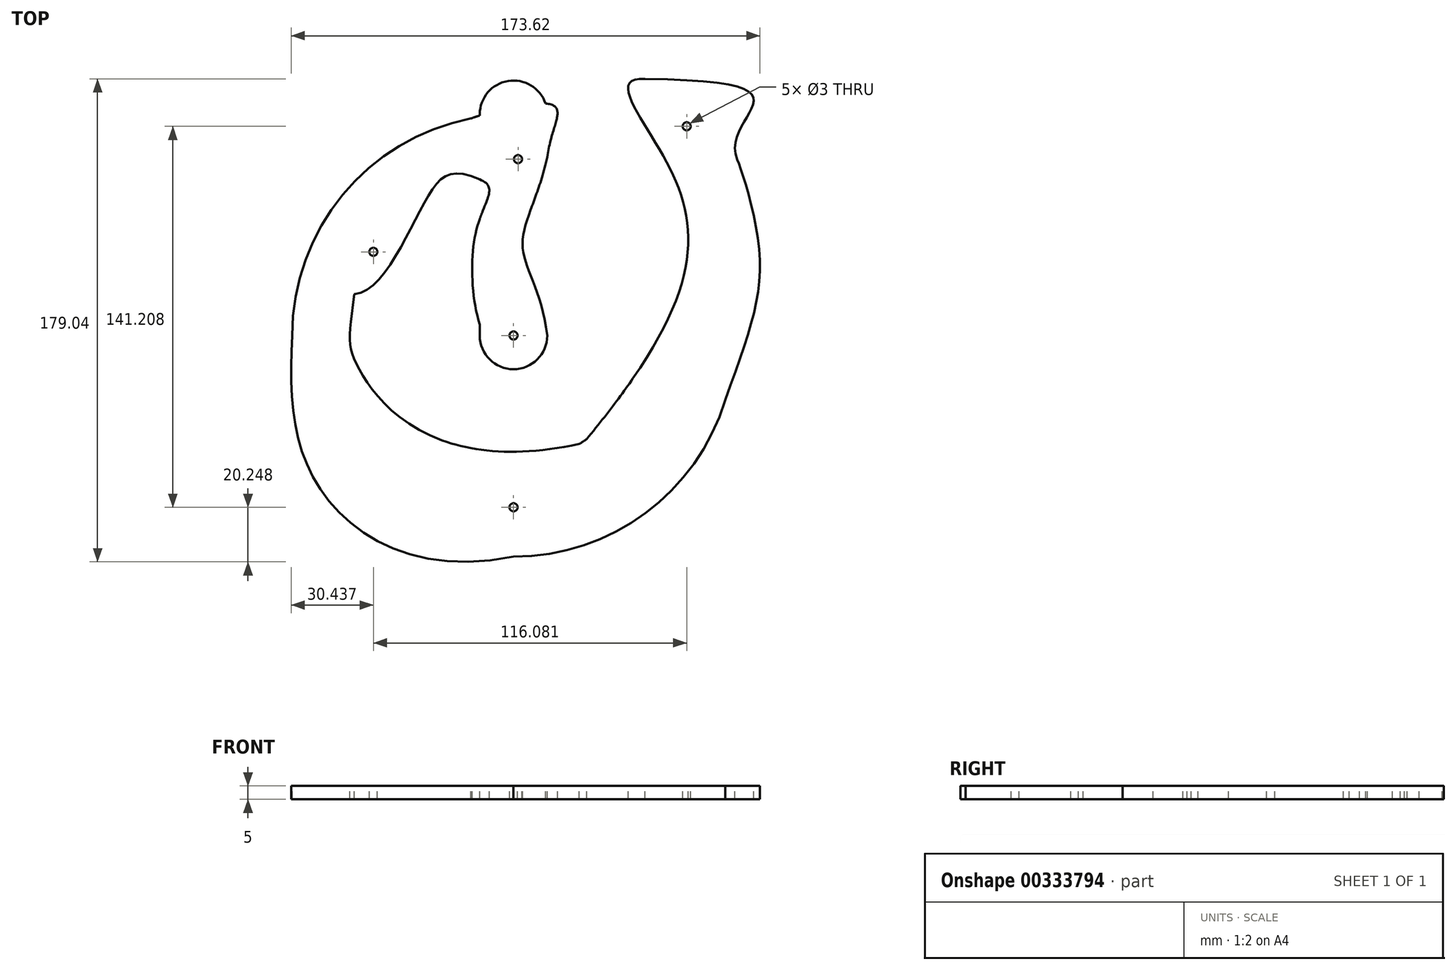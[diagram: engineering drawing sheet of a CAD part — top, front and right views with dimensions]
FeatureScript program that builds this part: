
annotation { "Feature Type Name" : "Feature", "Feature Type Description" : "" }
export const myFeature = defineFeature(function(context is Context, id is Id, definition is map)
    precondition{}
    {
        {
            var Q0;
            Q0=qCreatedBy(makeId("Top.planeOp"),FACE);
            var sketch = newSketch(context, id + "F0", { "sketchPlane" : qUnion([Q0])});
            skLineSegment(sketch, "E0.bottom", {"start": v(100, 100) * mm, "end": v(-100, 100) * mm});
            skLineSegment(sketch, "E0.top", {"start": v(100, -100) * mm, "end": v(-100, -100) * mm});
            skLineSegment(sketch, "E0.left", {"start": v(100, 100) * mm, "end": v(100, -100) * mm});
            skLineSegment(sketch, "E0.right", {"start": v(-100, 100) * mm, "end": v(-100, -100) * mm});
            skPoint(sketch, "E0.middle", {"position": v(0, 0) * mm});
            skSolve(sketch);
        }
        {
            var Q0;
            Q0=qSketchRegion(id+"F0",true);
            extrude(context, id + "F1", {"entities" : qUnion([Q0]), "depth" : 5 * mm});
        }
        {
            var Q0;
            Q0=makeQuery(id+"F1.opExtrude","CAP_FACE",FACE,{"disambiguationData":[OSD([sQuery(id+"F0.wireOp",EDGE,"E0.bottom"),sQuery(id+"F0.wireOp",EDGE,"E0.top"),sQuery(id+"F0.wireOp",EDGE,"E0.left"),sQuery(id+"F0.wireOp",EDGE,"E0.right")])],"isStart":false});
            var sketch = newSketch(context, id + "F2", { "sketchPlane" : qUnion([Q0])});
            skCircle(sketch, "E1", {"center": v(0, 0) * mm, "radius": 1.5 * mm});
            skCircle(sketch, "E2", {"center": v(0, -63.66) * mm, "radius": 1.5 * mm});
            skCircle(sketch, "E3", {"center": v(64.16, 77.55) * mm, "radius": 1.5 * mm});
            skCircle(sketch, "E4", {"center": v(-51.92, 31.01) * mm, "radius": 1.5 * mm});
            skCircle(sketch, "E5", {"center": v(1.67, 65.37) * mm, "radius": 1.5 * mm});
            skSolve(sketch);
        }
        {
            var Q0;
            Q0=qSketchRegion(id+"F2",true);
            extrude(context, id + "F3", {"entities" : qUnion([Q0]), "operationType" : NewBodyOperationType.REMOVE, "endBound" : BoundingType.THROUGH_ALL, "oppositeDirection" : true, "depth" : 25 * mm});
        }
        {
            var Q0;
            Q0=makeQuery(id+"F1.opExtrude","CAP_FACE",FACE,{"disambiguationData":[OSD([sQuery(id+"F0.wireOp",EDGE,"E0.bottom"),sQuery(id+"F0.wireOp",EDGE,"E0.top"),sQuery(id+"F0.wireOp",EDGE,"E0.left"),sQuery(id+"F0.wireOp",EDGE,"E0.right")])],"isStart":false});
            var sketch = newSketch(context, id + "F4", { "sketchPlane" : qUnion([Q0])});
            skCircle(sketch, "E6", {"center": v(0, 0) * mm, "radius": 82 * mm});
            skCircle(sketch, "E7", {"center": v(0, 0) * mm, "radius": 47 * mm});
            skLineSegment(sketch, "E8", {"start": v(0, 0) * mm, "end": v(0, 82) * mm});
            skArc(sketch, "E9.0.startCap", {"start": v(12.5, 0) * mm, "mid": v(0, -12.5) * mm, "end": v(-12.5, 0) * mm});
            skArc(sketch, "E9.0.endCap", {"start": v(-12.5, 82) * mm, "mid": v(0, 94.5) * mm, "end": v(12.5, 82) * mm});
            skLineSegment(sketch, "E9.0.left", {"start": v(-12.5, 0) * mm, "end": v(-12.5, 82) * mm});
            skLineSegment(sketch, "E9.0.right", {"start": v(12.5, 0) * mm, "end": v(12.5, 82) * mm});
            skFitSpline(sketch, "E10", {"points": [v(12.5, 0) * mm, v(3.35, 33.35) * mm, v(12.5, 66.16) * mm], "startDerivative": vector(-11.7, 100.36) * mm, "endDerivative": vector(19.92, 92.42) * mm});
            skFitSpline(sketch, "E11", {"points": [v(12.5, 66.16) * mm, v(14.58, 85.35) * mm, v(-63.7, 51.65) * mm], "startDerivative": vector(14.38, 102.91) * mm, "endDerivative": vector(-91.17, -104.15) * mm});
            skFitSpline(sketch, "E12", {"points": [v(-82, 0) * mm, v(-72.9, -54.82) * mm, v(0, -82) * mm], "startDerivative": vector(-6.39, -135.62) * mm, "endDerivative": vector(204.5, 41.58) * mm});
            skFitSpline(sketch, "E13", {"points": [v(-58.96, 15.36) * mm, v(-58.3, -10.2) * mm, v(29.11, -39.07) * mm], "startDerivative": vector(-16.81, -133.56) * mm, "endDerivative": vector(270.2, 67.65) * mm});
            skFitSpline(sketch, "E14", {"points": [v(76.13, -30.46) * mm, v(91.08, 30.53) * mm, v(82.92, 65.12) * mm], "startDerivative": vector(50.66, 145.96) * mm, "endDerivative": vector(-10.79, 25.43) * mm});
            skFitSpline(sketch, "E15", {"points": [v(27.07, -38.42) * mm, v(55.72, 66.12) * mm, v(48.7, 95.08) * mm], "startDerivative": vector(194.49, 235.5) * mm, "endDerivative": vector(122.95, -9.46) * mm});
            skFitSpline(sketch, "E16", {"points": [v(48.7, 95.08) * mm, v(82.92, 65.12) * mm], "startDerivative": vector(206.67, -2.57) * mm, "endDerivative": vector(22.16, -51.74) * mm});
            skFitSpline(sketch, "E17", {"points": [v(-12.5, 57.87) * mm, v(-32.01, 51.02) * mm, v(-58.96, 15.36) * mm], "startDerivative": vector(-81.67, 35.6) * mm, "endDerivative": vector(-55.16, -3.88) * mm});
            skFitSpline(sketch, "E18", {"points": [v(-12.5, 57.87) * mm, v(-14.02, 37.91) * mm, v(7.36, -10.1) * mm], "startDerivative": vector(59.25, -24.3) * mm, "endDerivative": vector(96.35, 40.15) * mm});
            skSolve(sketch);
        }
        {
            var Q0;
            {var subQ0=sQuery(id+"F4.wireOp",EDGE,"E12");Q0=makeQuery(id+"F4.imprint","IMPRINT",FACE,{"disambiguationData":[TD([[makeQuery(id+"F4.imprint","IMPRINT",EDGE,{"derivedFrom":subQ0}),-1.0]])]});}
            var Q1;
            {var subQ5=sQuery(id+"F4.wireOp",EDGE,"E17");Q1=makeQuery(id+"F4.imprint","IMPRINT",FACE,{"disambiguationData":[TD([[makeQuery(id+"F4.imprint","IMPRINT",EDGE,{"derivedFrom":subQ5}),1.0]])]});}
            var Q2;
            {var subQ1=sQuery(id+"F4.wireOp",EDGE,"E7");var subQ4=sQuery(id+"F4.wireOp",EDGE,"E9.0.left");var subQ9=makeQuery(id+"F4.imprint","INTERSECT",VERTEX,{"derivedFrom":[subQ1,subQ4]});Q2=makeQuery(id+"F4.imprint","IMPRINT",FACE,{"disambiguationData":[TD([[makeQuery(id+"F4.imprint","IMPRINT",EDGE,{"disambiguationData":[TD([[subQ9,-1.0]])],"derivedFrom":subQ1}),1.0]])]});}
            var Q3;
            {var subQ0=sQuery(id+"F4.wireOp",EDGE,"E18");var subQ1=sQuery(id+"F4.wireOp",EDGE,"E7");var subQ2=makeQuery(id+"F4.imprint","INTERSECT",VERTEX,{"derivedFrom":[subQ1,subQ0]});Q3=makeQuery(id+"F4.imprint","IMPRINT",FACE,{"disambiguationData":[TD([[makeQuery(id+"F4.imprint","IMPRINT",EDGE,{"disambiguationData":[TD([[subQ2,-1.0]])],"derivedFrom":subQ1}),-1.0]])]});}
            var Q4;
            {var subQ0=sQuery(id+"F4.wireOp",EDGE,"E18");var subQ1=sQuery(id+"F4.wireOp",EDGE,"E7");var subQ2=makeQuery(id+"F4.imprint","INTERSECT",VERTEX,{"derivedFrom":[subQ1,subQ0]});Q4=makeQuery(id+"F4.imprint","IMPRINT",FACE,{"disambiguationData":[TD([[makeQuery(id+"F4.imprint","IMPRINT",EDGE,{"disambiguationData":[TD([[subQ2,-1.0]])],"derivedFrom":subQ1}),1.0]])]});}
            var Q5;
            {var subQ0=sQuery(id+"F4.wireOp",EDGE,"E10");var subQ1=sQuery(id+"F4.wireOp",EDGE,"E7");var subQ2=makeQuery(id+"F4.imprint","INTERSECT",VERTEX,{"derivedFrom":[subQ1,subQ0]});Q5=makeQuery(id+"F4.imprint","IMPRINT",FACE,{"disambiguationData":[TD([[makeQuery(id+"F4.imprint","IMPRINT",EDGE,{"disambiguationData":[TD([[subQ2,1.0]])],"derivedFrom":subQ1}),1.0]])]});}
            var Q6;
            {var subQ0=sQuery(id+"F4.wireOp",EDGE,"E10");var subQ1=sQuery(id+"F4.wireOp",EDGE,"E7");var subQ2=makeQuery(id+"F4.imprint","INTERSECT",VERTEX,{"derivedFrom":[subQ1,subQ0]});Q6=makeQuery(id+"F4.imprint","IMPRINT",FACE,{"disambiguationData":[TD([[makeQuery(id+"F4.imprint","IMPRINT",EDGE,{"disambiguationData":[TD([[subQ2,1.0]])],"derivedFrom":subQ1}),-1.0]])]});}
            var Q7;
            {var subQ0=sQuery(id+"F4.wireOp",EDGE,"E9.0.left");var subQ1=sQuery(id+"F4.wireOp",EDGE,"E9.0.endCap");var subQ2=makeQuery(id+"F4.imprint","INTERSECT",VERTEX,{"derivedFrom":[subQ1,subQ0]});Q7=makeQuery(id+"F4.imprint","IMPRINT",FACE,{"disambiguationData":[TD([[makeQuery(id+"F4.imprint","IMPRINT",EDGE,{"disambiguationData":[TD([[subQ2,-1.0]])],"derivedFrom":subQ1}),-1.0]])]});}
            var Q8;
            {var subQ0=sQuery(id+"F4.wireOp",EDGE,"E11");var subQ3=sQuery(id+"F4.wireOp",EDGE,"E6");var subQ4=makeQuery(id+"F4.imprint","INTERSECT",VERTEX,{"disambiguationData":[OD(1.0)],"derivedFrom":[subQ3,subQ0]});Q8=makeQuery(id+"F4.imprint","IMPRINT",FACE,{"disambiguationData":[TD([[makeQuery(id+"F4.imprint","IMPRINT",EDGE,{"disambiguationData":[TD([[subQ4,1.0]])],"derivedFrom":subQ3}),1.0]])]});}
            extrude(context, id + "F5", {"entities" : qUnion([Q0, Q1, Q2, Q3, Q4, Q5, Q6, Q7, Q8]), "operationType" : NewBodyOperationType.REMOVE, "endBound" : BoundingType.THROUGH_ALL, "oppositeDirection" : true, "depth" : 25 * mm});
        }
    });
